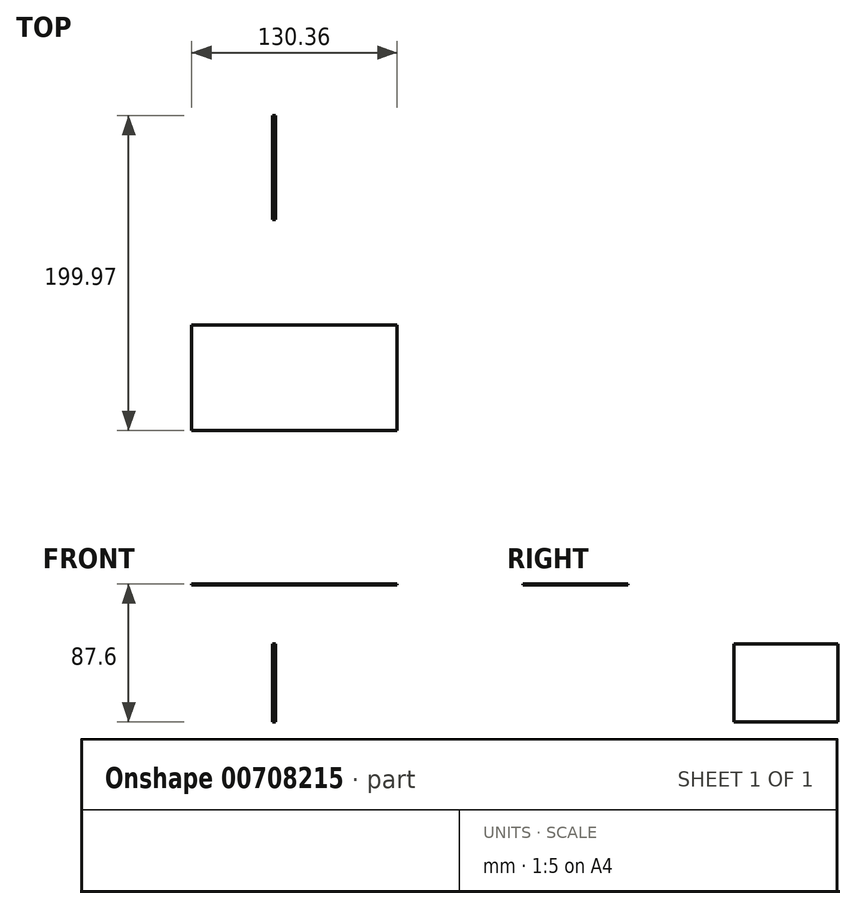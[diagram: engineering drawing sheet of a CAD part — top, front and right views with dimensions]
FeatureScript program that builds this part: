
annotation { "Feature Type Name" : "Feature", "Feature Type Description" : "" }
export const myFeature = defineFeature(function(context is Context, id is Id, definition is map)
    precondition{}
    {
        {
            var Q0;
            Q0=qCreatedBy(makeId("Top.planeOp"),FACE);
            var sketch = newSketch(context, id + "F0", { "sketchPlane" : qUnion([Q0])});
            skLineSegment(sketch, "E0.bottom", {"start": v(-53.2, -66.85) * mm, "end": v(77.16, -66.85) * mm});
            skLineSegment(sketch, "E0.top", {"start": v(-53.2, 0) * mm, "end": v(77.16, 0) * mm});
            skLineSegment(sketch, "E0.left", {"start": v(-53.2, -66.85) * mm, "end": v(-53.2, 0) * mm});
            skLineSegment(sketch, "E0.right", {"start": v(77.16, -66.85) * mm, "end": v(77.16, 0) * mm});
            skSolve(sketch);
        }
        {
            var Q0;
            Q0 = qSketchRegion(id + "F0", true);
            extrude(context, id + "F1", {"entities" : qUnion([Q0]), "depth" : 0.76 * mm, "offsetDistance" : 25.4 * mm});
        }
        {
            var Q0;
            Q0=qCreatedBy(makeId("Right.planeOp"),FACE);
            var sketch = newSketch(context, id + "F2", { "sketchPlane" : qUnion([Q0])});
            skLineSegment(sketch, "E1.bottom", {"start": v(67.19, -86.84) * mm, "end": v(133.12, -86.84) * mm});
            skLineSegment(sketch, "E1.top", {"start": v(67.19, -37.4) * mm, "end": v(133.12, -37.4) * mm});
            skLineSegment(sketch, "E1.left", {"start": v(67.19, -86.84) * mm, "end": v(67.19, -37.4) * mm});
            skLineSegment(sketch, "E1.right", {"start": v(133.12, -86.84) * mm, "end": v(133.12, -37.4) * mm});
            skSolve(sketch);
        }
        {
            var Q0;
            Q0 = qSketchRegion(id + "F2", true);
            extrude(context, id + "F3", {"entities" : qUnion([Q0]), "oppositeDirection" : true, "depth" : 1.78 * mm, "offsetDistance" : 25.4 * mm});
        }
    });
